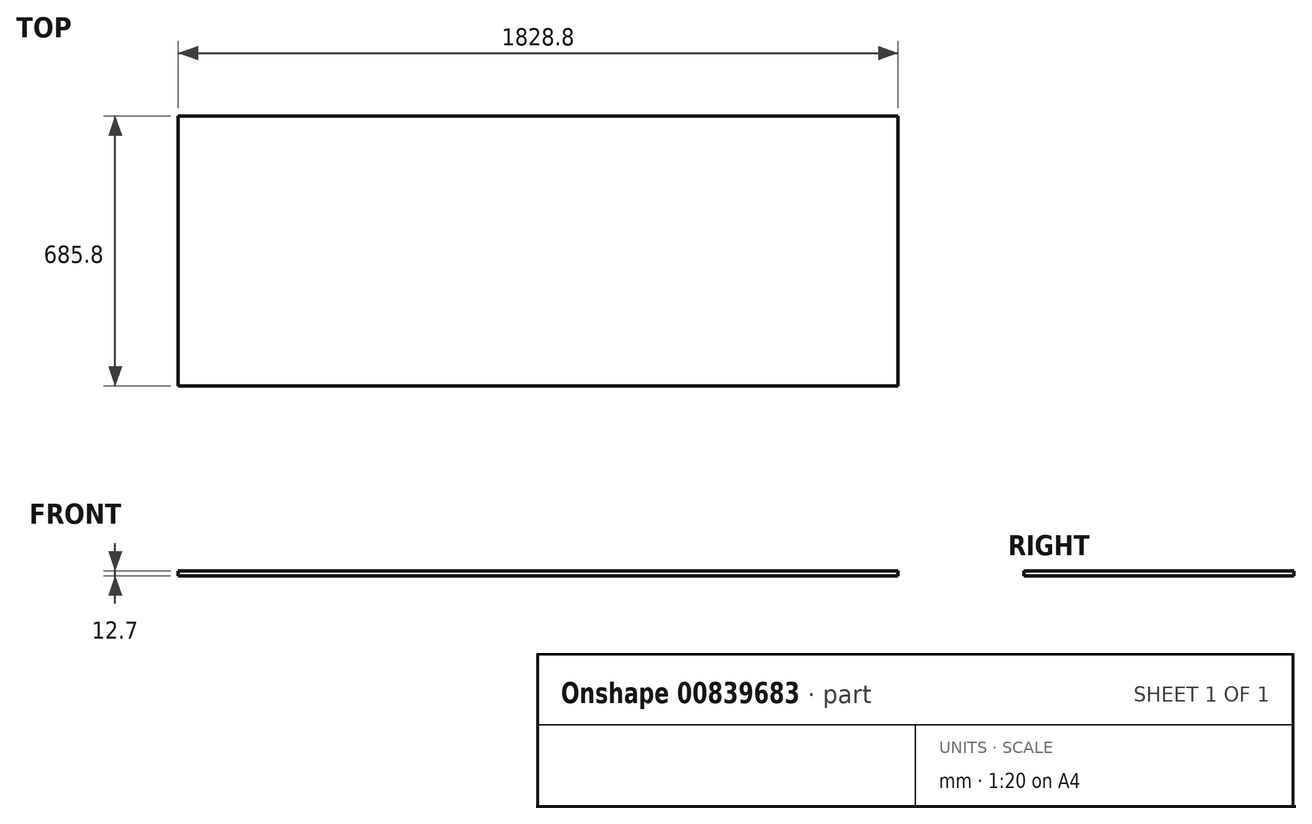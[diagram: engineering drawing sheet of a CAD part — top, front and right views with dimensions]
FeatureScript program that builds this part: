
annotation { "Feature Type Name" : "Feature", "Feature Type Description" : "" }
export const myFeature = defineFeature(function(context is Context, id is Id, definition is map)
    precondition{}
    {
        {
            var Q0;
            Q0=qCreatedBy(makeId("Top.planeOp"), FACE);
            var sketch = newSketch(context, id + "F0", { "sketchPlane" : qUnion([Q0])});
            skLineSegment(sketch, "E0.bottom", {"start": v(914.4, -342.9) * mm, "end": v(-914.4, -342.9) * mm});
            skLineSegment(sketch, "E0.top", {"start": v(914.4, 342.9) * mm, "end": v(-914.4, 342.9) * mm});
            skLineSegment(sketch, "E0.left", {"start": v(914.4, -342.9) * mm, "end": v(914.4, 342.9) * mm});
            skLineSegment(sketch, "E0.right", {"start": v(-914.4, -342.9) * mm, "end": v(-914.4, 342.9) * mm});
            skPoint(sketch, "E0.middle", {"position": v(0, 0) * mm});
            skSolve(sketch);
        }
        {
            var Q0;
            Q0 = qSketchRegion(id + "F0", true);
            extrude(context, id + "F1", {"entities" : qUnion([Q0]), "domain" : OperationDomain.MODEL, "flatOperationType" : FlatOperationType.REMOVE, "depth" : 12.7 * mm, "offsetDistance" : 25.4 * mm});
        }
    });
